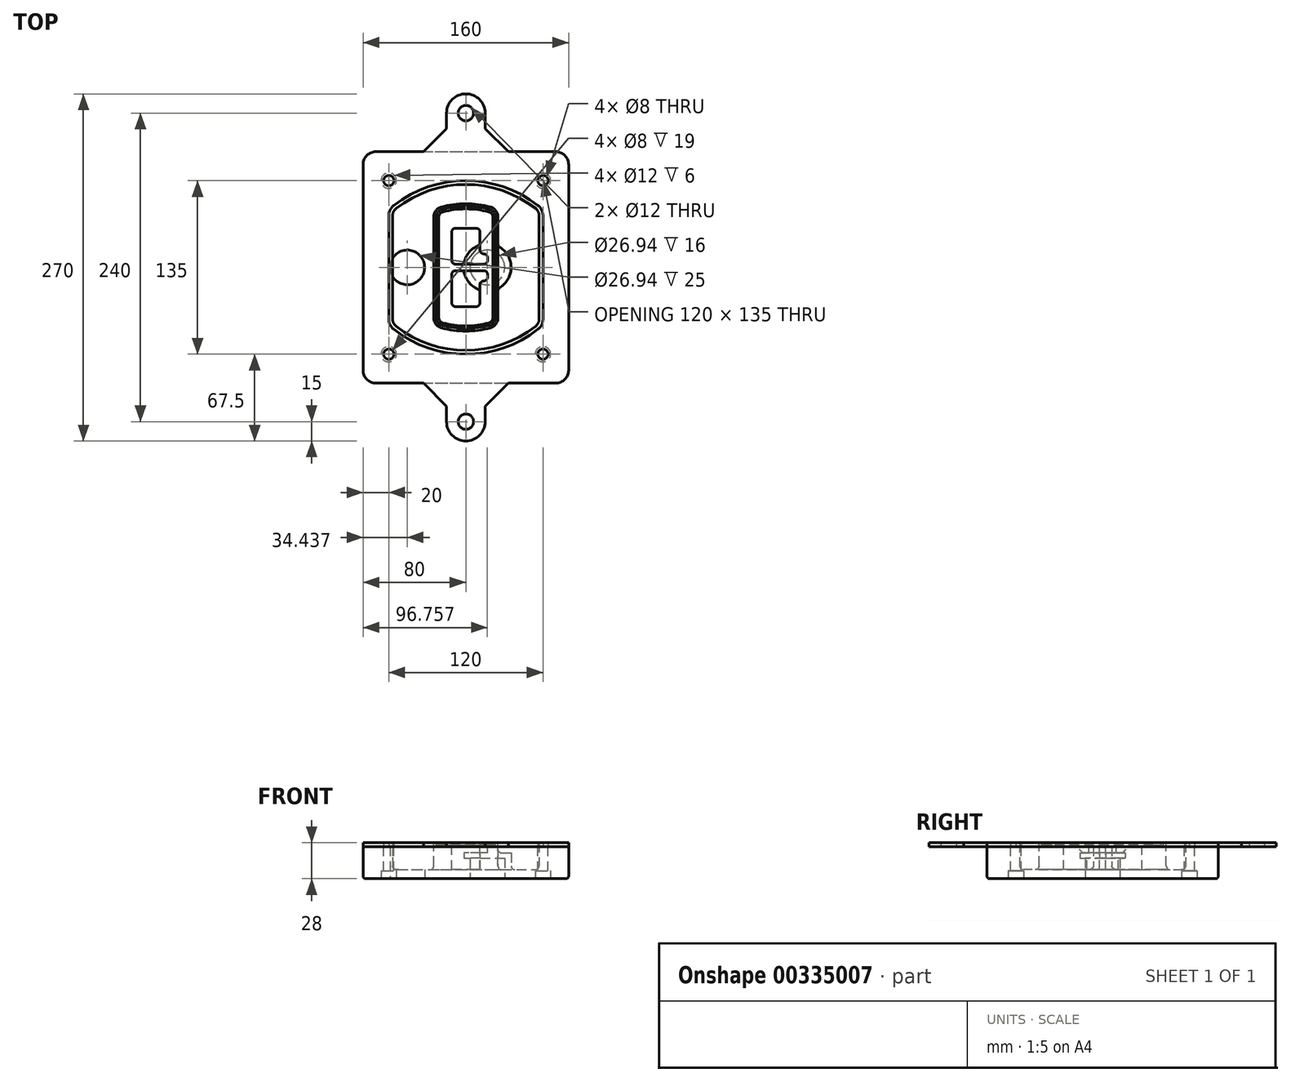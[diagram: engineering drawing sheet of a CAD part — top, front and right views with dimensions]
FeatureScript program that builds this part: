
annotation { "Feature Type Name" : "Feature", "Feature Type Description" : "" }
export const myFeature = defineFeature(function(context is Context, id is Id, definition is map)
    precondition{}
    {
        {
            var Q0;
            Q0=qCreatedBy(makeId("Top.planeOp"),FACE);
            var sketch = newSketch(context, id + "F0", { "sketchPlane" : qUnion([Q0])});
            skPoint(sketch, "E0.rect.middle", {"position": v(0, 0) * mm});
            skLineSegment(sketch, "E1.bottom", {"start": v(-70, -90) * mm, "end": v(70, -90) * mm});
            skLineSegment(sketch, "E1.top", {"start": v(-70, 90) * mm, "end": v(70, 90) * mm});
            skLineSegment(sketch, "E1.left", {"start": v(-80, -80) * mm, "end": v(-80, 80) * mm});
            skLineSegment(sketch, "E1.right", {"start": v(80, -80) * mm, "end": v(80, 80) * mm});
            skLineSegment(sketch, "E2", {"start": v(-80, 90) * mm, "end": v(80, -90) * mm, "construction": true});
            skLineSegment(sketch, "E3", {"start": v(80, 90) * mm, "end": v(-80, -90) * mm, "construction": true});
            skCircle(sketch, "E4", {"center": v(-60, 67.5) * mm, "radius": 4 * mm});
            skCircle(sketch, "E5", {"center": v(60, 67.5) * mm, "radius": 4 * mm});
            skCircle(sketch, "E6", {"center": v(60, -67.5) * mm, "radius": 4 * mm});
            skCircle(sketch, "E7", {"center": v(-60, -67.5) * mm, "radius": 4 * mm});
            skLineSegment(sketch, "E8", {"start": v(-60, 67.5) * mm, "end": v(60, 67.5) * mm, "construction": true});
            skLineSegment(sketch, "E9", {"start": v(60, 67.5) * mm, "end": v(60, -67.5) * mm, "construction": true});
            skLineSegment(sketch, "E10", {"start": v(60, -67.5) * mm, "end": v(-60, -67.5) * mm, "construction": true});
            skLineSegment(sketch, "E11", {"start": v(-60, -67.5) * mm, "end": v(-60, 67.5) * mm, "construction": true});
            skLineSegment(sketch, "E12", {"start": v(-60, 40.3) * mm, "end": v(-60, -40.3) * mm});
            skLineSegment(sketch, "E13", {"start": v(60, 40.3) * mm, "end": v(60, -40.3) * mm});
            skArc(sketch, "E14", {"start": v(56.15, 48.18) * mm, "mid": v(0, 67.5) * mm, "end": v(-56.15, 48.18) * mm});
            skArc(sketch, "E15", {"start": v(-56.15, -48.18) * mm, "mid": v(0, -67.5) * mm, "end": v(56.15, -48.18) * mm});
            skLineSegment(sketch, "E16", {"start": v(-60, 0) * mm, "end": v(60, 0) * mm, "construction": true});
            skPoint(sketch, "E17.visualSharp", {"position": v(-60, -45) * mm});
            skArc(sketch, "E17.filletArc", {"start": v(-60, -40.3) * mm, "mid": v(-58.99, -44.68) * mm, "end": v(-56.15, -48.18) * mm});
            skPoint(sketch, "E18.visualSharp", {"position": v(-60, 45) * mm});
            skArc(sketch, "E18.filletArc", {"start": v(-56.15, 48.18) * mm, "mid": v(-58.99, 44.68) * mm, "end": v(-60, 40.3) * mm});
            skPoint(sketch, "E19.visualSharp", {"position": v(60, 45) * mm});
            skArc(sketch, "E19.filletArc", {"start": v(60, 40.3) * mm, "mid": v(58.99, 44.68) * mm, "end": v(56.15, 48.18) * mm});
            skPoint(sketch, "E20.visualSharp", {"position": v(60, -45) * mm});
            skArc(sketch, "E20.filletArc", {"start": v(56.15, -48.18) * mm, "mid": v(58.99, -44.68) * mm, "end": v(60, -40.3) * mm});
            skPoint(sketch, "E21.visualSharp", {"position": v(-80, 90) * mm});
            skArc(sketch, "E21.filletArc", {"start": v(-70, 90) * mm, "mid": v(-77.07, 87.07) * mm, "end": v(-80, 80) * mm});
            skPoint(sketch, "E22.visualSharp", {"position": v(80, 90) * mm});
            skArc(sketch, "E22.filletArc", {"start": v(80, 80) * mm, "mid": v(77.07, 87.07) * mm, "end": v(70, 90) * mm});
            skPoint(sketch, "E23.visualSharp", {"position": v(80, -90) * mm});
            skArc(sketch, "E23.filletArc", {"start": v(70, -90) * mm, "mid": v(77.07, -87.07) * mm, "end": v(80, -80) * mm});
            skPoint(sketch, "E24.visualSharp", {"position": v(-80, -90) * mm});
            skArc(sketch, "E24.filletArc", {"start": v(-80, -80) * mm, "mid": v(-77.07, -87.07) * mm, "end": v(-70, -90) * mm});
            skArc(sketch, "E25.0", {"start": v(57, 40.3) * mm, "mid": v(56.3, 43.36) * mm, "end": v(54.3, 45.81) * mm});
            skLineSegment(sketch, "E25.1", {"start": v(57, 40.3) * mm, "end": v(57, -40.3) * mm});
            skArc(sketch, "E25.2", {"start": v(54.3, -45.81) * mm, "mid": v(56.3, -43.36) * mm, "end": v(57, -40.3) * mm});
            skArc(sketch, "E25.3", {"start": v(-54.3, -45.81) * mm, "mid": v(0, -64.5) * mm, "end": v(54.3, -45.81) * mm});
            skArc(sketch, "E25.4", {"start": v(-57, -40.3) * mm, "mid": v(-56.3, -43.36) * mm, "end": v(-54.3, -45.81) * mm});
            skArc(sketch, "E25.5", {"start": v(54.3, 45.81) * mm, "mid": v(0, 64.5) * mm, "end": v(-54.3, 45.81) * mm});
            skLineSegment(sketch, "E25.6", {"start": v(-57, 40.3) * mm, "end": v(-57, -40.3) * mm});
            skArc(sketch, "E25.7", {"start": v(-54.3, 45.81) * mm, "mid": v(-56.3, 43.36) * mm, "end": v(-57, 40.3) * mm});
            skArc(sketch, "E26.0", {"start": v(-58.62, 51.33) * mm, "mid": v(-62.58, 46.43) * mm, "end": v(-64, 40.3) * mm});
            skArc(sketch, "E26.1", {"start": v(58.62, 51.33) * mm, "mid": v(0, 71.5) * mm, "end": v(-58.62, 51.33) * mm});
            skArc(sketch, "E26.2", {"start": v(64, 40.3) * mm, "mid": v(62.58, 46.43) * mm, "end": v(58.62, 51.33) * mm});
            skLineSegment(sketch, "E26.3", {"start": v(64, 40.3) * mm, "end": v(64, -40.3) * mm});
            skArc(sketch, "E26.4", {"start": v(58.62, -51.33) * mm, "mid": v(62.58, -46.43) * mm, "end": v(64, -40.3) * mm});
            skLineSegment(sketch, "E26.5", {"start": v(-64, 40.3) * mm, "end": v(-64, -40.3) * mm});
            skArc(sketch, "E26.6", {"start": v(-58.62, -51.33) * mm, "mid": v(0, -71.5) * mm, "end": v(58.62, -51.33) * mm});
            skArc(sketch, "E26.7", {"start": v(-64, -40.3) * mm, "mid": v(-62.58, -46.43) * mm, "end": v(-58.62, -51.33) * mm});
            skSolve(sketch);
        }
        {
            var Q0;
            Q0=makeQuery(id+"F0.imprint","IMPRINT",FACE,{"disambiguationData":[TD([[makeQuery(id+"F0.imprint","IMPRINT",EDGE,{"derivedFrom":sQuery(id+"F0.wireOp",EDGE,"E1.bottom")}),1.0]])]});
            var Q1;
            Q1=makeQuery(id+"F0.imprint","IMPRINT",FACE,{"disambiguationData":[TD([[makeQuery(id+"F0.imprint","IMPRINT",EDGE,{"derivedFrom":sQuery(id+"F0.wireOp",EDGE,"E12")}),1.0]])]});
            var Q2;
            Q2=makeQuery(id+"F0.imprint","IMPRINT",FACE,{"disambiguationData":[TD([[makeQuery(id+"F0.imprint","IMPRINT",EDGE,{"derivedFrom":sQuery(id+"F0.wireOp",EDGE,"E25.0")}),1.0]])]});
            var Q3;
            Q3=makeQuery(id+"F0.imprint","IMPRINT",FACE,{"disambiguationData":[TD([[makeQuery(id+"F0.imprint","IMPRINT",EDGE,{"derivedFrom":sQuery(id+"F0.wireOp",EDGE,"E12")}),-1.0]])]});
            extrude(context, id + "F1", {"entities" : qUnion([Q0, Q1, Q2, Q3]), "oppositeDirection" : true, "depth" : 25 * mm});
        }
        {
            var Q0;
            Q0=makeQuery(id+"F0.imprint","IMPRINT",FACE,{"disambiguationData":[TD([[makeQuery(id+"F0.imprint","IMPRINT",EDGE,{"derivedFrom":sQuery(id+"F0.wireOp",EDGE,"E12")}),1.0]])]});
            var Q1;
            Q1 = qSketchRegion(id + "F16", true);
            extrude(context, id + "F2", {"entities" : qUnion([Q0, Q1]), "operationType" : NewBodyOperationType.ADD, "depth" : 3 * mm});
        }
        {
            var Q0;
            Q0=makeQuery(id+"F0.imprint","IMPRINT",FACE,{"disambiguationData":[TD([[makeQuery(id+"F0.imprint","IMPRINT",EDGE,{"derivedFrom":sQuery(id+"F0.wireOp",EDGE,"E25.0")}),1.0]])]});
            extrude(context, id + "F3", {"entities" : qUnion([Q0]), "operationType" : NewBodyOperationType.REMOVE, "oppositeDirection" : true, "depth" : 18 * mm});
        }
        {
            var Q0;
            Q0=makeQuery(id+"F2.opExtrude","CAP_FACE",FACE,{"disambiguationData":[OSD([sQuery(id+"F0.wireOp",EDGE,"E12"),sQuery(id+"F0.wireOp",EDGE,"E13"),sQuery(id+"F0.wireOp",EDGE,"E14"),sQuery(id+"F0.wireOp",EDGE,"E15"),sQuery(id+"F0.wireOp",EDGE,"E17.filletArc"),sQuery(id+"F0.wireOp",EDGE,"E18.filletArc"),sQuery(id+"F0.wireOp",EDGE,"E19.filletArc"),sQuery(id+"F0.wireOp",EDGE,"E20.filletArc"),sQuery(id+"F0.wireOp",EDGE,"E25.0"),sQuery(id+"F0.wireOp",EDGE,"E25.1"),sQuery(id+"F0.wireOp",EDGE,"E25.2"),sQuery(id+"F0.wireOp",EDGE,"E25.3"),sQuery(id+"F0.wireOp",EDGE,"E25.4"),sQuery(id+"F0.wireOp",EDGE,"E25.5"),sQuery(id+"F0.wireOp",EDGE,"E25.6"),sQuery(id+"F0.wireOp",EDGE,"E25.7")])],"isStart":false});
            var sketch = newSketch(context, id + "F4", { "sketchPlane" : qUnion([Q0])});
            skArc(sketch, "E27.0", {"start": v(-19.08, -46.97) * mm, "mid": v(0, -49.5) * mm, "end": v(19.08, -46.97) * mm});
            skArc(sketch, "E28.0", {"start": v(19.08, 46.97) * mm, "mid": v(0, 49.5) * mm, "end": v(-19.08, 46.97) * mm});
            skLineSegment(sketch, "E29", {"start": v(-25, 39.25) * mm, "end": v(-25, -39.25) * mm});
            skLineSegment(sketch, "E30", {"start": v(25, 39.25) * mm, "end": v(25, -39.25) * mm});
            skLineSegment(sketch, "E31", {"start": v(-25, 45.1) * mm, "end": v(25, 45.1) * mm, "construction": true});
            skLineSegment(sketch, "E32", {"start": v(-25, -45.1) * mm, "end": v(25, -45.1) * mm, "construction": true});
            skPoint(sketch, "E33.visualSharp", {"position": v(-25, 45.1) * mm});
            skArc(sketch, "E33.filletArc", {"start": v(-19.08, 46.97) * mm, "mid": v(-23.35, 44.11) * mm, "end": v(-25, 39.25) * mm});
            skPoint(sketch, "E34.visualSharp", {"position": v(25, 45.1) * mm});
            skArc(sketch, "E34.filletArc", {"start": v(25, 39.25) * mm, "mid": v(23.35, 44.11) * mm, "end": v(19.08, 46.97) * mm});
            skPoint(sketch, "E35.visualSharp", {"position": v(25, -45.1) * mm});
            skArc(sketch, "E35.filletArc", {"start": v(19.08, -46.97) * mm, "mid": v(23.35, -44.11) * mm, "end": v(25, -39.25) * mm});
            skPoint(sketch, "E36.visualSharp", {"position": v(-25, -45.1) * mm});
            skArc(sketch, "E36.filletArc", {"start": v(-25, -39.25) * mm, "mid": v(-23.35, -44.11) * mm, "end": v(-19.08, -46.97) * mm});
            skArc(sketch, "E37.0", {"start": v(54.3, 45.81) * mm, "mid": v(0, 64.5) * mm, "end": v(-54.3, 45.81) * mm});
            skArc(sketch, "E37.1", {"start": v(-54.3, 45.81) * mm, "mid": v(-56.3, 43.36) * mm, "end": v(-57, 40.3) * mm});
            skLineSegment(sketch, "E37.2", {"start": v(-57, 40.3) * mm, "end": v(-57, -40.3) * mm});
            skArc(sketch, "E37.3", {"start": v(-57, -40.3) * mm, "mid": v(-56.3, -43.36) * mm, "end": v(-54.3, -45.81) * mm});
            skArc(sketch, "E37.4", {"start": v(-54.3, -45.81) * mm, "mid": v(0, -64.5) * mm, "end": v(54.3, -45.81) * mm});
            skArc(sketch, "E37.5", {"start": v(54.3, -45.81) * mm, "mid": v(56.3, -43.36) * mm, "end": v(57, -40.3) * mm});
            skLineSegment(sketch, "E37.6", {"start": v(57, 40.3) * mm, "end": v(57, -40.3) * mm});
            skArc(sketch, "E37.7", {"start": v(57, 40.3) * mm, "mid": v(56.3, 43.36) * mm, "end": v(54.3, 45.81) * mm});
            skLineSegment(sketch, "E38.0", {"start": v(23, 39.25) * mm, "end": v(23, -39.25) * mm});
            skArc(sketch, "E38.1", {"start": v(18.56, -45.04) * mm, "mid": v(21.76, -42.9) * mm, "end": v(23, -39.25) * mm});
            skArc(sketch, "E38.2", {"start": v(-18.56, -45.04) * mm, "mid": v(0, -47.5) * mm, "end": v(18.56, -45.04) * mm});
            skArc(sketch, "E38.3", {"start": v(-23, -39.25) * mm, "mid": v(-21.76, -42.9) * mm, "end": v(-18.56, -45.04) * mm});
            skLineSegment(sketch, "E38.4", {"start": v(-23, 39.25) * mm, "end": v(-23, -39.25) * mm});
            skArc(sketch, "E38.5", {"start": v(23, 39.25) * mm, "mid": v(21.76, 42.9) * mm, "end": v(18.56, 45.04) * mm});
            skArc(sketch, "E38.6", {"start": v(-18.56, 45.04) * mm, "mid": v(-21.76, 42.9) * mm, "end": v(-23, 39.25) * mm});
            skArc(sketch, "E38.7", {"start": v(18.56, 45.04) * mm, "mid": v(0, 47.5) * mm, "end": v(-18.56, 45.04) * mm});
            skArc(sketch, "E39.0", {"start": v(21, 39.25) * mm, "mid": v(20.18, 41.68) * mm, "end": v(18.04, 43.1) * mm});
            skLineSegment(sketch, "E39.1", {"start": v(21, 39.25) * mm, "end": v(21, -39.25) * mm});
            skArc(sketch, "E39.2", {"start": v(18.04, -43.1) * mm, "mid": v(20.18, -41.68) * mm, "end": v(21, -39.25) * mm});
            skArc(sketch, "E39.3", {"start": v(-18.04, -43.1) * mm, "mid": v(0, -45.5) * mm, "end": v(18.04, -43.1) * mm});
            skArc(sketch, "E39.4", {"start": v(-21, -39.25) * mm, "mid": v(-20.18, -41.68) * mm, "end": v(-18.04, -43.1) * mm});
            skArc(sketch, "E39.5", {"start": v(18.04, 43.1) * mm, "mid": v(0, 45.5) * mm, "end": v(-18.04, 43.1) * mm});
            skLineSegment(sketch, "E39.6", {"start": v(-21, 39.25) * mm, "end": v(-21, -39.25) * mm});
            skArc(sketch, "E39.7", {"start": v(-18.04, 43.1) * mm, "mid": v(-20.18, 41.68) * mm, "end": v(-21, 39.25) * mm});
            skLineSegment(sketch, "E40", {"start": v(-25, 0) * mm, "end": v(25, 0) * mm, "construction": true});
            skLineSegment(sketch, "E41", {"start": v(-11, 5.5) * mm, "end": v(-11, 27.5) * mm});
            skLineSegment(sketch, "E42", {"start": v(-8, 30.5) * mm, "end": v(8, 30.5) * mm});
            skLineSegment(sketch, "E43", {"start": v(11, 27.5) * mm, "end": v(11, 13.5) * mm});
            skLineSegment(sketch, "E44", {"start": v(14, 10.5) * mm, "end": v(14, 10.5) * mm});
            skLineSegment(sketch, "E45", {"start": v(17, 7.5) * mm, "end": v(17, 5.5) * mm});
            skLineSegment(sketch, "E46", {"start": v(14, 2.5) * mm, "end": v(-8, 2.5) * mm});
            skPoint(sketch, "E47.visualSharp", {"position": v(-11, 30.5) * mm});
            skArc(sketch, "E47.filletArc", {"start": v(-8, 30.5) * mm, "mid": v(-10.12, 29.62) * mm, "end": v(-11, 27.5) * mm});
            skPoint(sketch, "E48.visualSharp", {"position": v(11, 30.5) * mm});
            skArc(sketch, "E48.filletArc", {"start": v(11, 27.5) * mm, "mid": v(10.12, 29.62) * mm, "end": v(8, 30.5) * mm});
            skPoint(sketch, "E49.visualSharp", {"position": v(11, 10.5) * mm});
            skArc(sketch, "E49.filletArc", {"start": v(11, 13.5) * mm, "mid": v(11.88, 11.38) * mm, "end": v(14, 10.5) * mm});
            skPoint(sketch, "E50.visualSharp", {"position": v(17, 10.5) * mm});
            skArc(sketch, "E50.filletArc", {"start": v(17, 7.5) * mm, "mid": v(16.12, 9.62) * mm, "end": v(14, 10.5) * mm});
            skPoint(sketch, "E51.visualSharp", {"position": v(17, 2.5) * mm});
            skArc(sketch, "E51.filletArc", {"start": v(14, 2.5) * mm, "mid": v(16.12, 3.38) * mm, "end": v(17, 5.5) * mm});
            skPoint(sketch, "E52.visualSharp", {"position": v(-11, 2.5) * mm});
            skArc(sketch, "E52.filletArc", {"start": v(-11, 5.5) * mm, "mid": v(-10.12, 3.38) * mm, "end": v(-8, 2.5) * mm});
            skLineSegment(sketch, "E53.0.MirrorCS", {"start": v(14, -2.5) * mm, "end": v(-8, -2.5) * mm});
            skArc(sketch, "E54.0.MirrorCS", {"start": v(-11, -5.5) * mm, "mid": v(-10.12, -3.38) * mm, "end": v(-8, -2.5) * mm});
            skLineSegment(sketch, "E55.0.MirrorCS", {"start": v(-11, -5.5) * mm, "end": v(-11, -27.5) * mm});
            skArc(sketch, "E56.0.MirrorCS", {"start": v(-8, -30.5) * mm, "mid": v(-10.12, -29.62) * mm, "end": v(-11, -27.5) * mm});
            skLineSegment(sketch, "E57.0.MirrorCS", {"start": v(-8, -30.5) * mm, "end": v(8, -30.5) * mm});
            skArc(sketch, "E58.0.MirrorCS", {"start": v(11, -27.5) * mm, "mid": v(10.12, -29.62) * mm, "end": v(8, -30.5) * mm});
            skLineSegment(sketch, "E59.0.MirrorCS", {"start": v(11, -27.5) * mm, "end": v(11, -13.5) * mm});
            skArc(sketch, "E60.0.MirrorCS", {"start": v(11, -13.5) * mm, "mid": v(11.88, -11.38) * mm, "end": v(14, -10.5) * mm});
            skArc(sketch, "E61.0.MirrorCS", {"start": v(17, -7.5) * mm, "mid": v(16.12, -9.62) * mm, "end": v(14, -10.5) * mm});
            skLineSegment(sketch, "E62.0.MirrorCS", {"start": v(17, -7.5) * mm, "end": v(17, -5.5) * mm});
            skArc(sketch, "E63.0.MirrorCS", {"start": v(14, -2.5) * mm, "mid": v(16.12, -3.38) * mm, "end": v(17, -5.5) * mm});
            skSolve(sketch);
        }
        {
            var Q0;
            Q0=makeQuery(id+"F4.imprint","IMPRINT",FACE,{"disambiguationData":[TD([[makeQuery(id+"F4.imprint","IMPRINT",EDGE,{"derivedFrom":sQuery(id+"F4.wireOp",EDGE,"E27.0")}),1.0]])]});
            var Q1;
            Q1=makeQuery(id+"F4.imprint","IMPRINT",FACE,{"disambiguationData":[TD([[makeQuery(id+"F4.imprint","IMPRINT",EDGE,{"derivedFrom":sQuery(id+"F4.wireOp",EDGE,"E38.0")}),-1.0]])]});
            var Q2;
            Q2=makeQuery(id+"F4.imprint","IMPRINT",FACE,{"disambiguationData":[TD([[makeQuery(id+"F4.imprint","IMPRINT",EDGE,{"derivedFrom":sQuery(id+"F4.wireOp",EDGE,"E39.0")}),1.0]])]});
            extrude(context, id + "F5", {"entities" : qUnion([Q0, Q1, Q2]), "operationType" : NewBodyOperationType.ADD, "endBound" : BoundingType.UP_TO_NEXT, "oppositeDirection" : true, "depth" : 25 * mm});
        }
        {
            var Q0;
            Q0=makeQuery(id+"F4.imprint","IMPRINT",FACE,{"disambiguationData":[TD([[makeQuery(id+"F4.imprint","IMPRINT",EDGE,{"derivedFrom":sQuery(id+"F4.wireOp",EDGE,"E38.0")}),-1.0]])]});
            extrude(context, id + "F6", {"entities" : qUnion([Q0]), "operationType" : NewBodyOperationType.REMOVE, "oppositeDirection" : true, "depth" : 2 * mm});
        }
        {
            var Q0;
            Q0=makeQuery(id+"F1.opExtrude","CAP_FACE",FACE,{"disambiguationData":[OSD([sQuery(id+"F0.wireOp",EDGE,"E1.bottom"),sQuery(id+"F0.wireOp",EDGE,"E1.top"),sQuery(id+"F0.wireOp",EDGE,"E1.left"),sQuery(id+"F0.wireOp",EDGE,"E1.right"),sQuery(id+"F0.wireOp",EDGE,"E4"),sQuery(id+"F0.wireOp",EDGE,"E5"),sQuery(id+"F0.wireOp",EDGE,"E6"),sQuery(id+"F0.wireOp",EDGE,"E7"),sQuery(id+"F0.wireOp",EDGE,"E21.filletArc"),sQuery(id+"F0.wireOp",EDGE,"E22.filletArc"),sQuery(id+"F0.wireOp",EDGE,"E23.filletArc"),sQuery(id+"F0.wireOp",EDGE,"E24.filletArc")])],"isStart":false});
            var sketch = newSketch(context, id + "F7", { "sketchPlane" : qUnion([Q0])});
            skCircle(sketch, "E64", {"center": v(16.76, 0) * mm, "radius": 13.47 * mm});
            skCircle(sketch, "E65", {"center": v(-45.56, 0) * mm, "radius": 13.47 * mm});
            skLineSegment(sketch, "E66", {"start": v(80, 0) * mm, "end": v(-80, 0) * mm});
            skCircle(sketch, "E67", {"center": v(16.76, 0) * mm, "radius": 18.47 * mm});
            skCircle(sketch, "E68", {"center": v(60, -67.5) * mm, "radius": 6 * mm});
            skCircle(sketch, "E69", {"center": v(-60, -67.5) * mm, "radius": 6 * mm});
            skCircle(sketch, "E70", {"center": v(-60, 67.5) * mm, "radius": 6 * mm});
            skCircle(sketch, "E71", {"center": v(60, 67.5) * mm, "radius": 6 * mm});
            skSolve(sketch);
        }
        {
            var Q0;
            {var subQ1=sQuery(id+"F7.wireOp",EDGE,"E66");var subQ4=sQuery(id+"F7.wireOp",EDGE,"E64");var subQ6=makeQuery(id+"F7.imprint","INTERSECT",VERTEX,{"disambiguationData":[OD(0.0)],"derivedFrom":[subQ4,subQ1]});Q0=makeQuery(id+"F7.imprint","IMPRINT",FACE,{"disambiguationData":[TD([[makeQuery(id+"F7.imprint","IMPRINT",EDGE,{"disambiguationData":[TD([[subQ6,-1.0]])],"derivedFrom":subQ4}),-1.0]])]});}
            var Q1;
            {var subQ0=sQuery(id+"F7.wireOp",EDGE,"E66");var subQ1=sQuery(id+"F7.wireOp",EDGE,"E64");var subQ3=makeQuery(id+"F7.imprint","INTERSECT",VERTEX,{"disambiguationData":[OD(0.0)],"derivedFrom":[subQ1,subQ0]});Q1=makeQuery(id+"F7.imprint","IMPRINT",FACE,{"disambiguationData":[TD([[makeQuery(id+"F7.imprint","IMPRINT",EDGE,{"disambiguationData":[TD([[subQ3,-1.0]])],"derivedFrom":subQ1}),1.0]])]});}
            var Q2;
            {var subQ0=sQuery(id+"F7.wireOp",EDGE,"E66");var subQ1=sQuery(id+"F7.wireOp",EDGE,"E64");var subQ3=makeQuery(id+"F7.imprint","INTERSECT",VERTEX,{"disambiguationData":[OD(0.0)],"derivedFrom":[subQ1,subQ0]});Q2=makeQuery(id+"F7.imprint","IMPRINT",FACE,{"disambiguationData":[TD([[makeQuery(id+"F7.imprint","IMPRINT",EDGE,{"disambiguationData":[TD([[subQ3,1.0]])],"derivedFrom":subQ1}),1.0]])]});}
            var Q3;
            {var subQ1=sQuery(id+"F7.wireOp",EDGE,"E66");var subQ4=sQuery(id+"F7.wireOp",EDGE,"E64");var subQ6=makeQuery(id+"F7.imprint","INTERSECT",VERTEX,{"disambiguationData":[OD(0.0)],"derivedFrom":[subQ4,subQ1]});Q3=makeQuery(id+"F7.imprint","IMPRINT",FACE,{"disambiguationData":[TD([[makeQuery(id+"F7.imprint","IMPRINT",EDGE,{"disambiguationData":[TD([[subQ6,1.0]])],"derivedFrom":subQ4}),-1.0]])]});}
            extrude(context, id + "F8", {"entities" : qUnion([Q0, Q1, Q2, Q3]), "operationType" : NewBodyOperationType.ADD, "oppositeDirection" : true, "depth" : 20 * mm});
        }
        {
            var Q0;
            {var subQ0=sQuery(id+"F7.wireOp",EDGE,"E66");var subQ1=sQuery(id+"F7.wireOp",EDGE,"E64");var subQ3=makeQuery(id+"F7.imprint","INTERSECT",VERTEX,{"disambiguationData":[OD(0.0)],"derivedFrom":[subQ1,subQ0]});Q0=makeQuery(id+"F7.imprint","IMPRINT",FACE,{"disambiguationData":[TD([[makeQuery(id+"F7.imprint","IMPRINT",EDGE,{"disambiguationData":[TD([[subQ3,-1.0]])],"derivedFrom":subQ1}),1.0]])]});}
            var Q1;
            {var subQ0=sQuery(id+"F7.wireOp",EDGE,"E66");var subQ1=sQuery(id+"F7.wireOp",EDGE,"E64");var subQ3=makeQuery(id+"F7.imprint","INTERSECT",VERTEX,{"disambiguationData":[OD(0.0)],"derivedFrom":[subQ1,subQ0]});Q1=makeQuery(id+"F7.imprint","IMPRINT",FACE,{"disambiguationData":[TD([[makeQuery(id+"F7.imprint","IMPRINT",EDGE,{"disambiguationData":[TD([[subQ3,1.0]])],"derivedFrom":subQ1}),1.0]])]});}
            extrude(context, id + "F9", {"entities" : qUnion([Q0, Q1]), "operationType" : NewBodyOperationType.REMOVE, "oppositeDirection" : true, "depth" : 16 * mm});
        }
        {
            var Q0;
            {var subQ0=sQuery(id+"F7.wireOp",EDGE,"E66");var subQ1=sQuery(id+"F7.wireOp",EDGE,"E65");var subQ3=makeQuery(id+"F7.imprint","INTERSECT",VERTEX,{"disambiguationData":[OD(0.0)],"derivedFrom":[subQ1,subQ0]});Q0=makeQuery(id+"F7.imprint","IMPRINT",FACE,{"disambiguationData":[TD([[makeQuery(id+"F7.imprint","IMPRINT",EDGE,{"disambiguationData":[TD([[subQ3,-1.0]])],"derivedFrom":subQ1}),1.0]])]});}
            var Q1;
            {var subQ0=sQuery(id+"F7.wireOp",EDGE,"E66");var subQ1=sQuery(id+"F7.wireOp",EDGE,"E65");var subQ3=makeQuery(id+"F7.imprint","INTERSECT",VERTEX,{"disambiguationData":[OD(0.0)],"derivedFrom":[subQ1,subQ0]});Q1=makeQuery(id+"F7.imprint","IMPRINT",FACE,{"disambiguationData":[TD([[makeQuery(id+"F7.imprint","IMPRINT",EDGE,{"disambiguationData":[TD([[subQ3,1.0]])],"derivedFrom":subQ1}),1.0]])]});}
            extrude(context, id + "F10", {"entities" : qUnion([Q0, Q1]), "operationType" : NewBodyOperationType.REMOVE, "oppositeDirection" : true, "depth" : 25 * mm});
        }
        {
            var Q0;
            Q0=makeQuery(id+"F7.imprint","IMPRINT",FACE,{"disambiguationData":[TD([[makeQuery(id+"F7.imprint","IMPRINT",EDGE,{"derivedFrom":sQuery(id+"F7.wireOp",EDGE,"E68")}),1.0]])]});
            var Q1;
            Q1=makeQuery(id+"F7.imprint","IMPRINT",FACE,{"disambiguationData":[TD([[makeQuery(id+"F7.imprint","IMPRINT",EDGE,{"derivedFrom":makeQuery(id+"F1.opExtrude","CAP_EDGE",EDGE,{"disambiguationData":[OSD([sQuery(id+"F0.wireOp",EDGE,"E5")])],"isStart":false})}),-1.0]])]});
            var Q2;
            Q2=makeQuery(id+"F7.imprint","IMPRINT",FACE,{"disambiguationData":[TD([[makeQuery(id+"F7.imprint","IMPRINT",EDGE,{"derivedFrom":sQuery(id+"F7.wireOp",EDGE,"E69")}),1.0]])]});
            var Q3;
            Q3=makeQuery(id+"F7.imprint","IMPRINT",FACE,{"disambiguationData":[TD([[makeQuery(id+"F7.imprint","IMPRINT",EDGE,{"derivedFrom":makeQuery(id+"F1.opExtrude","CAP_EDGE",EDGE,{"disambiguationData":[OSD([sQuery(id+"F0.wireOp",EDGE,"E4")])],"isStart":false})}),-1.0]])]});
            var Q4;
            Q4=makeQuery(id+"F7.imprint","IMPRINT",FACE,{"disambiguationData":[TD([[makeQuery(id+"F7.imprint","IMPRINT",EDGE,{"derivedFrom":sQuery(id+"F7.wireOp",EDGE,"E70")}),1.0]])]});
            var Q5;
            Q5=makeQuery(id+"F7.imprint","IMPRINT",FACE,{"disambiguationData":[TD([[makeQuery(id+"F7.imprint","IMPRINT",EDGE,{"derivedFrom":makeQuery(id+"F1.opExtrude","CAP_EDGE",EDGE,{"disambiguationData":[OSD([sQuery(id+"F0.wireOp",EDGE,"E7")])],"isStart":false})}),-1.0]])]});
            var Q6;
            Q6=makeQuery(id+"F7.imprint","IMPRINT",FACE,{"disambiguationData":[TD([[makeQuery(id+"F7.imprint","IMPRINT",EDGE,{"derivedFrom":sQuery(id+"F7.wireOp",EDGE,"E71")}),1.0]])]});
            var Q7;
            Q7=makeQuery(id+"F7.imprint","IMPRINT",FACE,{"disambiguationData":[TD([[makeQuery(id+"F7.imprint","IMPRINT",EDGE,{"derivedFrom":makeQuery(id+"F1.opExtrude","CAP_EDGE",EDGE,{"disambiguationData":[OSD([sQuery(id+"F0.wireOp",EDGE,"E6")])],"isStart":false})}),-1.0]])]});
            extrude(context, id + "F11", {"entities" : qUnion([Q0, Q1, Q2, Q3, Q4, Q5, Q6, Q7]), "operationType" : NewBodyOperationType.REMOVE, "oppositeDirection" : true, "depth" : 6 * mm});
        }
        {
            var Q0;
            Q0=makeQuery(id+"F9.boolean.opBoolean","COPY",FACE,{"derivedFrom":makeQuery(id+"F9.opExtrude","CAP_FACE",FACE,{"disambiguationData":[OSD([sQuery(id+"F7.wireOp",EDGE,"E64")])],"isStart":false})});
            var sketch = newSketch(context, id + "F12", { "sketchPlane" : qUnion([Q0])});
            skArc(sketch, "E72.0", {"start": v(11, 17.55) * mm, "mid": v(2.57, 11.82) * mm, "end": v(-1.54, 2.5) * mm});
            skArc(sketch, "E72.1", {"start": v(-1.54, -2.5) * mm, "mid": v(2.57, -11.82) * mm, "end": v(11, -17.55) * mm});
            skLineSegment(sketch, "E73", {"start": v(-1.54, -2.5) * mm, "end": v(14, -2.5) * mm});
            skLineSegment(sketch, "E74.0", {"start": v(14, 2.5) * mm, "end": v(-1.54, 2.5) * mm});
            skArc(sketch, "E74.1", {"start": v(14, 2.5) * mm, "mid": v(16.12, 3.38) * mm, "end": v(17, 5.5) * mm});
            skLineSegment(sketch, "E74.2", {"start": v(17, 7.5) * mm, "end": v(17, 5.5) * mm});
            skArc(sketch, "E74.3", {"start": v(17, 7.5) * mm, "mid": v(16.12, 9.62) * mm, "end": v(14, 10.5) * mm});
            skArc(sketch, "E74.4", {"start": v(11, 13.5) * mm, "mid": v(11.88, 11.38) * mm, "end": v(14, 10.5) * mm});
            skLineSegment(sketch, "E74.5", {"start": v(11, 17.55) * mm, "end": v(11, 13.5) * mm});
            skLineSegment(sketch, "E74.7", {"start": v(14, -2.5) * mm, "end": v(-1.54, -2.5) * mm});
            skArc(sketch, "E74.8", {"start": v(14, -2.5) * mm, "mid": v(16.12, -3.38) * mm, "end": v(17, -5.5) * mm});
            skLineSegment(sketch, "E74.9", {"start": v(17, -7.5) * mm, "end": v(17, -5.5) * mm});
            skArc(sketch, "E74.10", {"start": v(17, -7.5) * mm, "mid": v(16.12, -9.62) * mm, "end": v(14, -10.5) * mm});
            skArc(sketch, "E74.11", {"start": v(11, -13.5) * mm, "mid": v(11.88, -11.38) * mm, "end": v(14, -10.5) * mm});
            skLineSegment(sketch, "E74.12", {"start": v(11, -17.55) * mm, "end": v(11, -13.5) * mm});
            skPoint(sketch, "E75.orphan", {"position": v(11, -27.5) * mm});
            skPoint(sketch, "E76.orphan", {"position": v(-8, -2.5) * mm});
            skPoint(sketch, "E77.orphan", {"position": v(-8, 2.5) * mm});
            skPoint(sketch, "E78.orphan", {"position": v(11, 27.5) * mm});
            skSolve(sketch);
        }
        {
            var Q0;
            {var subQ7=sQuery(id+"F12.wireOp",EDGE,"E72.0");var subQ14=sQuery(id+"F12.wireOp",EDGE,"E72.1");var subQ16=sQuery(id+"F12.wireOp",EDGE,"E74.1");var subQ18=sQuery(id+"F12.wireOp",EDGE,"E74.8");Q0=qUnion([makeQuery(id+"F12.imprint","IMPRINT",FACE,{"disambiguationData":[TD([[makeQuery(id+"F12.imprint","IMPRINT",EDGE,{"derivedFrom":subQ7}),1.0]])]}),makeQuery(id+"F12.imprint","IMPRINT",FACE,{"disambiguationData":[TD([[makeQuery(id+"F12.imprint","IMPRINT",EDGE,{"derivedFrom":subQ14}),1.0]])]}),makeQuery(id+"F12.imprint","IMPRINT",FACE,{"disambiguationData":[TD([[makeQuery(id+"F12.imprint","IMPRINT",EDGE,{"derivedFrom":subQ16}),1.0]])]}),makeQuery(id+"F12.imprint","IMPRINT",FACE,{"disambiguationData":[TD([[makeQuery(id+"F12.imprint","IMPRINT",EDGE,{"derivedFrom":subQ18}),-1.0]])]})]);}
            var Q1;
            Q1=makeQuery(id+"F5.boolean.opBoolean","SPLIT",FACE,{"disambiguationData":[TD([makeQuery(id+"F5.opExtrude","SWEPT_FACE",FACE,{"disambiguationData":[OSD([sQuery(id+"F4.wireOp",EDGE,"E41")])]})])],"derivedFrom":makeQuery(id+"F3.boolean.opBoolean","COPY",FACE,{"derivedFrom":makeQuery(id+"F3.opExtrude","CAP_FACE",FACE,{"disambiguationData":[OSD([sQuery(id+"F0.wireOp",EDGE,"E25.0"),sQuery(id+"F0.wireOp",EDGE,"E25.1"),sQuery(id+"F0.wireOp",EDGE,"E25.2"),sQuery(id+"F0.wireOp",EDGE,"E25.3"),sQuery(id+"F0.wireOp",EDGE,"E25.4"),sQuery(id+"F0.wireOp",EDGE,"E25.5"),sQuery(id+"F0.wireOp",EDGE,"E25.6"),sQuery(id+"F0.wireOp",EDGE,"E25.7")])],"isStart":false})})});
            extrude(context, id + "F13", {"entities" : qUnion([Q0]), "operationType" : NewBodyOperationType.REMOVE, "endBound" : BoundingType.UP_TO_SURFACE, "endBoundEntityFace" : qUnion([Q1]), "depth" : 25 * mm});
        }
        {
            var Q0;
            Q0=makeQuery(id+"F3.boolean.opBoolean","COPY",EDGE,{"derivedFrom":makeQuery(id+"F3.opExtrude","CAP_EDGE",EDGE,{"disambiguationData":[OSD([sQuery(id+"F0.wireOp",EDGE,"E25.6")])],"isStart":false})});
            var Q1;
            Q1=makeQuery(id+"F8.boolean.opBoolean","INTERSECT",EDGE,{"derivedFrom":[makeQuery(id+"F5.opExtrude","SWEPT_FACE",FACE,{"disambiguationData":[OSD([sQuery(id+"F4.wireOp",EDGE,"E30")])]}),makeQuery(id+"F8.opExtrude","CAP_FACE",FACE,{"disambiguationData":[OSD([sQuery(id+"F7.wireOp",EDGE,"E67")])],"isStart":false})]});
            var Q2;
            Q2=makeQuery(id+"F8.boolean.opBoolean","INTERSECT",EDGE,{"disambiguationData":[OD(1.0)],"derivedFrom":[makeQuery(id+"F5.opExtrude","SWEPT_FACE",FACE,{"disambiguationData":[OSD([sQuery(id+"F4.wireOp",EDGE,"E30")])]}),makeQuery(id+"F8.opExtrude","SWEPT_FACE",FACE,{"disambiguationData":[OSD([sQuery(id+"F7.wireOp",EDGE,"E67")])]})]});
            var Q3;
            {var subQ0=sQuery(id+"F4.wireOp",EDGE,"E30");Q3=makeQuery(id+"F8.boolean.opBoolean","SPLIT",EDGE,{"disambiguationData":[TD([makeQuery(id+"F5.opExtrude","SWEPT_FACE",FACE,{"disambiguationData":[OSD([sQuery(id+"F4.wireOp",EDGE,"E35.filletArc")])]})])],"derivedFrom":makeQuery(id+"F5.opExtrude","CAP_EDGE",EDGE,{"disambiguationData":[OSD([subQ0])],"isStart":false})});}
            var Q4;
            {var subQ0=sQuery(id+"F0.wireOp",EDGE,"E25.7");var subQ1=sQuery(id+"F0.wireOp",EDGE,"E25.1");var subQ2=sQuery(id+"F0.wireOp",EDGE,"E25.6");var subQ3=sQuery(id+"F0.wireOp",EDGE,"E25.5");var subQ4=sQuery(id+"F0.wireOp",EDGE,"E25.4");var subQ5=sQuery(id+"F0.wireOp",EDGE,"E25.0");var subQ6=sQuery(id+"F0.wireOp",EDGE,"E25.2");var subQ7=sQuery(id+"F0.wireOp",EDGE,"E25.3");Q4=makeQuery(id+"F8.boolean.opBoolean","INTERSECT",EDGE,{"derivedFrom":[makeQuery(id+"F5.boolean.opBoolean","SPLIT",FACE,{"disambiguationData":[TD([makeQuery(id+"F2.opExtrude","SWEPT_FACE",FACE,{"disambiguationData":[OSD([subQ5])]})])],"derivedFrom":makeQuery(id+"F3.boolean.opBoolean","COPY",FACE,{"derivedFrom":makeQuery(id+"F3.opExtrude","CAP_FACE",FACE,{"disambiguationData":[OSD([subQ5,subQ1,subQ6,subQ7,subQ4,subQ3,subQ2,subQ0])],"isStart":false})})}),makeQuery(id+"F8.opExtrude","SWEPT_FACE",FACE,{"disambiguationData":[OSD([sQuery(id+"F7.wireOp",EDGE,"E67")])]})]});}
            var Q5;
            Q5=makeQuery(id+"F8.boolean.opBoolean","INTERSECT",EDGE,{"disambiguationData":[OD(0.0)],"derivedFrom":[makeQuery(id+"F5.opExtrude","SWEPT_FACE",FACE,{"disambiguationData":[OSD([sQuery(id+"F4.wireOp",EDGE,"E30")])]}),makeQuery(id+"F8.opExtrude","SWEPT_FACE",FACE,{"disambiguationData":[OSD([sQuery(id+"F7.wireOp",EDGE,"E67")])]})]});
            fillet(context, id + "F14", {"entities" : qUnion([Q0, Q1, Q2, Q3, Q4, Q5]), "radius" : 3 * mm, "tangentPropagation" : true, "allowEdgeOverflow" : false});
        }
        {
            var Q0;
            Q0=makeQuery(id+"F1.opExtrude","CAP_EDGE",EDGE,{"disambiguationData":[OSD([sQuery(id+"F0.wireOp",EDGE,"E1.bottom")])],"isStart":false});
            fillet(context, id + "F15", {"entities" : qUnion([Q0]), "radius" : 2 * mm, "tangentPropagation" : true, "allowEdgeOverflow" : false});
        }
        {
            var Q0;
            {var subQ0=sQuery(id+"F0.wireOp",EDGE,"E21.filletArc");var subQ1=sQuery(id+"F0.wireOp",EDGE,"E7");var subQ2=sQuery(id+"F0.wireOp",EDGE,"E6");var subQ3=sQuery(id+"F0.wireOp",EDGE,"E5");var subQ4=sQuery(id+"F0.wireOp",EDGE,"E4");var subQ5=sQuery(id+"F0.wireOp",EDGE,"E22.filletArc");var subQ6=sQuery(id+"F0.wireOp",EDGE,"E1.bottom");var subQ7=sQuery(id+"F0.wireOp",EDGE,"E1.right");var subQ8=sQuery(id+"F0.wireOp",EDGE,"E1.top");var subQ9=sQuery(id+"F0.wireOp",EDGE,"E1.left");var subQ10=sQuery(id+"F0.wireOp",EDGE,"E23.filletArc");var subQ11=sQuery(id+"F0.wireOp",EDGE,"E24.filletArc");Q0=makeQuery(id+"F2.boolean.opBoolean","SPLIT",FACE,{"disambiguationData":[TD([makeQuery(id+"F1.opExtrude","SWEPT_FACE",FACE,{"disambiguationData":[OSD([subQ6])]})])],"derivedFrom":makeQuery(id+"F1.opExtrude","CAP_FACE",FACE,{"disambiguationData":[OSD([subQ6,subQ8,subQ9,subQ7,subQ4,subQ3,subQ2,subQ1,subQ0,subQ5,subQ10,subQ11])],"isStart":true})});}
            var sketch = newSketch(context, id + "F16", { "sketchPlane" : qUnion([Q0])});
            skLineSegment(sketch, "E79", {"start": v(-33, 90) * mm, "end": v(-15, 108) * mm});
            skLineSegment(sketch, "E80", {"start": v(-15, 108) * mm, "end": v(-15, 120) * mm});
            skLineSegment(sketch, "E81", {"start": v(15, 120) * mm, "end": v(15, 108) * mm});
            skLineSegment(sketch, "E82", {"start": v(15, 108) * mm, "end": v(33, 90) * mm});
            skArc(sketch, "E83", {"start": v(15, 120) * mm, "mid": v(0, 135) * mm, "end": v(-15, 120) * mm});
            skLineSegment(sketch, "E84", {"start": v(0, 120) * mm, "end": v(0, 90) * mm, "construction": true});
            skCircle(sketch, "E85", {"center": v(0, 120) * mm, "radius": 6 * mm});
            skLineSegment(sketch, "E86", {"start": v(-80, 0) * mm, "end": v(80, 0) * mm, "construction": true});
            skLineSegment(sketch, "E87.MirrorCS", {"start": v(0, -120) * mm, "end": v(0, -90) * mm, "construction": true});
            skLineSegment(sketch, "E88.MirrorCS", {"start": v(15, -120) * mm, "end": v(15, -108) * mm});
            skLineSegment(sketch, "E89.MirrorCS", {"start": v(15, -108) * mm, "end": v(33, -90) * mm});
            skArc(sketch, "E90.MirrorCS", {"start": v(15, -120) * mm, "mid": v(0, -135) * mm, "end": v(-15, -120) * mm});
            skCircle(sketch, "E91.MirrorC", {"center": v(0, -120) * mm, "radius": 6 * mm});
            skLineSegment(sketch, "E92.MirrorCS", {"start": v(-33, -90) * mm, "end": v(-15, -108) * mm});
            skLineSegment(sketch, "E93.MirrorCS", {"start": v(-15, -108) * mm, "end": v(-15, -120) * mm});
            skSolve(sketch);
        }
        {
            var Q0;
            Q0=makeQuery(id+"F16.imprint","IMPRINT",FACE,{"disambiguationData":[TD([[makeQuery(id+"F16.imprint","IMPRINT",EDGE,{"derivedFrom":sQuery(id+"F16.wireOp",EDGE,"E88.MirrorCS")}),1.0]])]});
            var Q1;
            {var subQ1=sQuery(id+"F16.wireOp",EDGE,"E79");Q1=makeQuery(id+"F16.imprint","IMPRINT",FACE,{"disambiguationData":[TD([[makeQuery(id+"F16.imprint","IMPRINT",EDGE,{"derivedFrom":subQ1}),-1.0]])]});}
            var Q2;
            Q2=makeQuery(id+"F16.imprint","IMPRINT",FACE,{"disambiguationData":[TD([[makeQuery(id+"F16.imprint","IMPRINT",EDGE,{"derivedFrom":makeQuery(id+"F1.opExtrude","CAP_EDGE",EDGE,{"disambiguationData":[OSD([sQuery(id+"F0.wireOp",EDGE,"E1.left")])],"isStart":true})}),-1.0]])]});
            var Q3;
            Q3=makeQuery(id+"F2.opExtrude","CAP_FACE",FACE,{"disambiguationData":[OSD([sQuery(id+"F0.wireOp",EDGE,"E12"),sQuery(id+"F0.wireOp",EDGE,"E13"),sQuery(id+"F0.wireOp",EDGE,"E14"),sQuery(id+"F0.wireOp",EDGE,"E15"),sQuery(id+"F0.wireOp",EDGE,"E17.filletArc"),sQuery(id+"F0.wireOp",EDGE,"E18.filletArc"),sQuery(id+"F0.wireOp",EDGE,"E19.filletArc"),sQuery(id+"F0.wireOp",EDGE,"E20.filletArc"),sQuery(id+"F0.wireOp",EDGE,"E25.0"),sQuery(id+"F0.wireOp",EDGE,"E25.1"),sQuery(id+"F0.wireOp",EDGE,"E25.2"),sQuery(id+"F0.wireOp",EDGE,"E25.3"),sQuery(id+"F0.wireOp",EDGE,"E25.4"),sQuery(id+"F0.wireOp",EDGE,"E25.5"),sQuery(id+"F0.wireOp",EDGE,"E25.6"),sQuery(id+"F0.wireOp",EDGE,"E25.7")])],"isStart":false});
            extrude(context, id + "F17", {"entities" : qUnion([Q0, Q1, Q2]), "endBound" : BoundingType.UP_TO_SURFACE, "endBoundEntityFace" : qUnion([Q3]), "depth" : 25 * mm});
        }
    });
